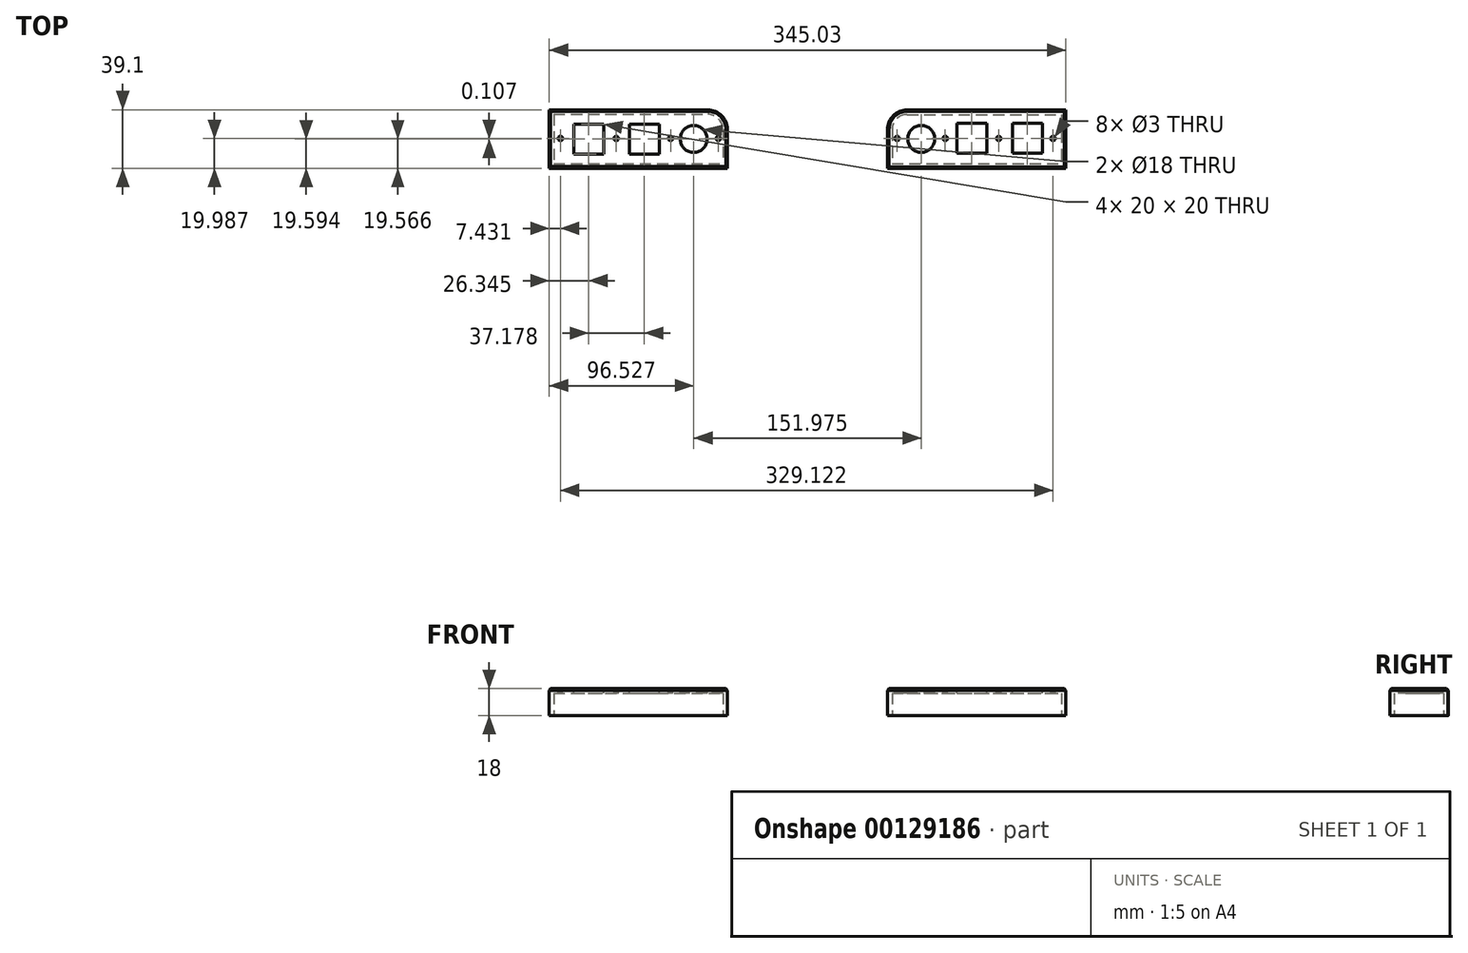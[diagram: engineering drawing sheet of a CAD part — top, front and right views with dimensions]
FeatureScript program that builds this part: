
annotation { "Feature Type Name" : "Feature", "Feature Type Description" : "" }
export const myFeature = defineFeature(function(context is Context, id is Id, definition is map)
    precondition{}
    {
        {
            var Q0;
            Q0=qCreatedBy(makeId("Top.planeOp"),FACE);
            var sketch = newSketch(context, id + "F0", { "sketchPlane" : qUnion([Q0])});
            skLineSegment(sketch, "E0.bottom", {"start": v(66.11, 78.9) * mm, "end": v(169.11, 78.9) * mm});
            skLineSegment(sketch, "E0.top", {"start": v(56.11, 45.9) * mm, "end": v(169.11, 45.9) * mm});
            skLineSegment(sketch, "E0.left", {"start": v(56.11, 68.9) * mm, "end": v(56.11, 45.9) * mm});
            skLineSegment(sketch, "E0.right", {"start": v(169.11, 78.9) * mm, "end": v(169.11, 45.9) * mm});
            skLineSegment(sketch, "E1.bottom", {"start": v(-169.92, 79) * mm, "end": v(-66.92, 79) * mm});
            skLineSegment(sketch, "E1.top", {"start": v(-169.92, 46) * mm, "end": v(-56.92, 46) * mm});
            skLineSegment(sketch, "E1.left", {"start": v(-169.92, 79) * mm, "end": v(-169.92, 46) * mm});
            skLineSegment(sketch, "E1.right", {"start": v(-56.92, 69) * mm, "end": v(-56.92, 46) * mm});
            skPoint(sketch, "E2.visualSharp", {"position": v(-56.92, 79) * mm});
            skArc(sketch, "E2.filletArc", {"start": v(-56.92, 69) * mm, "mid": v(-59.85, 76.07) * mm, "end": v(-66.92, 79) * mm});
            skPoint(sketch, "E3.visualSharp", {"position": v(56.11, 78.9) * mm});
            skArc(sketch, "E3.filletArc", {"start": v(66.11, 78.9) * mm, "mid": v(59.04, 75.97) * mm, "end": v(56.11, 68.9) * mm});
            skSolve(sketch);
        }
        {
            var Q0;
            Q0=qSketchRegion(id+"F0",true);
            extrude(context, id + "F1", {"entities" : qUnion([Q0]), "depth" : 5 * mm, "hasSecondDirection" : true, "secondDirectionOppositeDirection" : true, "secondDirectionDepth" : 10 * mm});
        }
        {
            var Q0;
            Q0=makeQuery(id+"F1.opExtrude","CAP_FACE",FACE,{"disambiguationData":[OSD([sQuery(id+"F0.wireOp",EDGE,"E0.bottom"),sQuery(id+"F0.wireOp",EDGE,"E0.top"),sQuery(id+"F0.wireOp",EDGE,"E0.left"),sQuery(id+"F0.wireOp",EDGE,"E0.right"),sQuery(id+"F0.wireOp",EDGE,"E3.filletArc")])],"isStart":true});
            var Q1;
            Q1=makeQuery(id+"F1.opExtrude","CAP_FACE",FACE,{"disambiguationData":[OSD([sQuery(id+"F0.wireOp",EDGE,"E1.bottom"),sQuery(id+"F0.wireOp",EDGE,"E1.top"),sQuery(id+"F0.wireOp",EDGE,"E1.left"),sQuery(id+"F0.wireOp",EDGE,"E1.right"),sQuery(id+"F0.wireOp",EDGE,"E2.filletArc")])],"isStart":true});
            shell(context, id + "F2", {"entities" : qUnion([Q0, Q1]), "thickness" : 3 * mm, "oppositeDirection" : true});
        }
        {
            var Q0;
            Q0=makeQuery(id+"F1.opExtrude","CAP_FACE",FACE,{"disambiguationData":[OSD([sQuery(id+"F0.wireOp",EDGE,"E0.bottom"),sQuery(id+"F0.wireOp",EDGE,"E0.top"),sQuery(id+"F0.wireOp",EDGE,"E0.left"),sQuery(id+"F0.wireOp",EDGE,"E0.right"),sQuery(id+"F0.wireOp",EDGE,"E3.filletArc")])],"isStart":false});
            cPlane(context, id + "F3", {"entities" : qUnion([Q0]), "cplaneType" : CPlaneType.OFFSET, "offset" : 25 * mm, "width" : 150 * mm, "height" : 150 * mm});
        }
        {
            var Q0;
            Q0=qCreatedBy(id+"F3.planeOp",FACE);
            var sketch = newSketch(context, id + "F4", { "sketchPlane" : qUnion([Q0])});
            skLineSegment(sketch, "E4.bottom", {"start": v(-156.58, 72.47) * mm, "end": v(-136.58, 72.47) * mm});
            skLineSegment(sketch, "E4.top", {"start": v(-156.58, 52.47) * mm, "end": v(-136.58, 52.47) * mm});
            skLineSegment(sketch, "E4.left", {"start": v(-156.58, 72.47) * mm, "end": v(-156.58, 52.47) * mm});
            skLineSegment(sketch, "E4.right", {"start": v(-136.58, 72.47) * mm, "end": v(-136.58, 52.47) * mm});
            skLineSegment(sketch, "E5.bottom", {"start": v(-119.4, 72.47) * mm, "end": v(-99.4, 72.47) * mm});
            skLineSegment(sketch, "E5.top", {"start": v(-119.4, 52.47) * mm, "end": v(-99.4, 52.47) * mm});
            skLineSegment(sketch, "E5.left", {"start": v(-119.4, 72.47) * mm, "end": v(-119.4, 52.47) * mm});
            skLineSegment(sketch, "E5.right", {"start": v(-99.4, 72.47) * mm, "end": v(-99.4, 52.47) * mm});
            skCircle(sketch, "E6", {"center": v(-76.4, 62.5) * mm, "radius": 9 * mm});
            skCircle(sketch, "E7", {"center": v(75.58, 62.6) * mm, "radius": 9 * mm});
            skLineSegment(sketch, "E8.bottom", {"start": v(99.27, 72.97) * mm, "end": v(119.27, 72.97) * mm});
            skLineSegment(sketch, "E8.top", {"start": v(99.27, 52.97) * mm, "end": v(119.27, 52.97) * mm});
            skLineSegment(sketch, "E8.left", {"start": v(99.27, 72.97) * mm, "end": v(99.27, 52.97) * mm});
            skLineSegment(sketch, "E8.right", {"start": v(119.27, 72.97) * mm, "end": v(119.27, 52.97) * mm});
            skLineSegment(sketch, "E9.bottom", {"start": v(136.45, 72.97) * mm, "end": v(156.45, 72.97) * mm});
            skLineSegment(sketch, "E9.top", {"start": v(136.45, 52.97) * mm, "end": v(156.45, 52.97) * mm});
            skLineSegment(sketch, "E9.left", {"start": v(136.45, 72.97) * mm, "end": v(136.45, 52.97) * mm});
            skLineSegment(sketch, "E9.right", {"start": v(156.45, 72.97) * mm, "end": v(156.45, 52.97) * mm});
            skSolve(sketch);
        }
        {
            var Q0;
            Q0=qSketchRegion(id+"F4",true);
            extrude(context, id + "F5", {"entities" : qUnion([Q0]), "operationType" : NewBodyOperationType.REMOVE, "oppositeDirection" : true, "depth" : 50 * mm});
        }
        {
            var Q0;
            Q0=makeQuery(id+"F1.opExtrude","CAP_FACE",FACE,{"disambiguationData":[OSD([sQuery(id+"F0.wireOp",EDGE,"E1.bottom"),sQuery(id+"F0.wireOp",EDGE,"E1.top"),sQuery(id+"F0.wireOp",EDGE,"E1.left"),sQuery(id+"F0.wireOp",EDGE,"E1.right"),sQuery(id+"F0.wireOp",EDGE,"E2.filletArc")])],"isStart":false});
            cPlane(context, id + "F6", {"entities" : qUnion([Q0]), "cplaneType" : CPlaneType.OFFSET, "offset" : 0 * mm, "width" : 150 * mm, "height" : 150 * mm});
        }
        {
            var Q0;
            Q0=qCreatedBy(id+"F6.planeOp",FACE);
            var sketch = newSketch(context, id + "F7", { "sketchPlane" : qUnion([Q0])});
            skPoint(sketch, "E10", {"position": v(-165.49, 62.89) * mm});
            skPoint(sketch, "E11", {"position": v(-128.13, 62.89) * mm});
            skPoint(sketch, "E12", {"position": v(-91.87, 62.89) * mm});
            skPoint(sketch, "E13", {"position": v(-59.97, 62.89) * mm});
            skPoint(sketch, "E14", {"position": v(59.47, 62.89) * mm});
            skPoint(sketch, "E15", {"position": v(91.64, 62.89) * mm});
            skPoint(sketch, "E16", {"position": v(127.36, 62.89) * mm});
            skPoint(sketch, "E17", {"position": v(163.63, 62.89) * mm});
            skSolve(sketch);
        }
        {
            var Q0;
            Q0=sQuery(id+"F7.wireOp",VERTEX,"E11");
            var Q1;
            Q1=sQuery(id+"F7.wireOp",VERTEX,"E17");
            var Q2;
            Q2=sQuery(id+"F7.wireOp",VERTEX,"E16");
            var Q3;
            Q3=sQuery(id+"F7.wireOp",VERTEX,"E10");
            var Q4;
            Q4=sQuery(id+"F7.wireOp",VERTEX,"E15");
            var Q5;
            Q5=sQuery(id+"F7.wireOp",VERTEX,"E14");
            var Q6;
            Q6=sQuery(id+"F7.wireOp",VERTEX,"E12");
            var Q7;
            Q7=sQuery(id+"F7.wireOp",VERTEX,"E13");
            var Q8;
            Q8=makeQuery(id+"F1.opExtrude","SWEPT_BODY",BODY,{"disambiguationData":[OSD([sQuery(id+"F0.wireOp",EDGE,"E0.bottom"),sQuery(id+"F0.wireOp",EDGE,"E0.top"),sQuery(id+"F0.wireOp",EDGE,"E0.left"),sQuery(id+"F0.wireOp",EDGE,"E0.right"),sQuery(id+"F0.wireOp",EDGE,"E3.filletArc")])]});
            var Q9;
            Q9=makeQuery(id+"F1.opExtrude","SWEPT_BODY",BODY,{"disambiguationData":[OSD([sQuery(id+"F0.wireOp",EDGE,"E1.bottom"),sQuery(id+"F0.wireOp",EDGE,"E1.top"),sQuery(id+"F0.wireOp",EDGE,"E1.left"),sQuery(id+"F0.wireOp",EDGE,"E1.right"),sQuery(id+"F0.wireOp",EDGE,"E2.filletArc")])]});
            hole(context, id + "F8", {"style" : HoleStyle.SIMPLE, "endStyle" : HoleEndStyle.BLIND, "holeDiameter" : 3 * mm, "holeDepth" : 40 * mm, "startFromSketch" : true, "locations" : qUnion([Q0, Q1, Q2, Q3, Q4, Q5, Q6, Q7]), "scope" : qUnion([Q8, Q9])});
        }
        {
            var Q0;
            Q0=makeQuery(id+"F1.opExtrude","CAP_EDGE",EDGE,{"disambiguationData":[OSD([sQuery(id+"F0.wireOp",EDGE,"E1.top")])],"isStart":false});
            var Q1;
            Q1=makeQuery(id+"F1.opExtrude","CAP_EDGE",EDGE,{"disambiguationData":[OSD([sQuery(id+"F0.wireOp",EDGE,"E1.left")])],"isStart":false});
            var Q2;
            Q2=makeQuery(id+"F1.opExtrude","CAP_EDGE",EDGE,{"disambiguationData":[OSD([sQuery(id+"F0.wireOp",EDGE,"E1.bottom")])],"isStart":false});
            var Q3;
            Q3=makeQuery(id+"F1.opExtrude","CAP_EDGE",EDGE,{"disambiguationData":[OSD([sQuery(id+"F0.wireOp",EDGE,"E0.left")])],"isStart":false});
            var Q4;
            Q4=makeQuery(id+"F1.opExtrude","CAP_EDGE",EDGE,{"disambiguationData":[OSD([sQuery(id+"F0.wireOp",EDGE,"E0.top")])],"isStart":false});
            var Q5;
            Q5=makeQuery(id+"F1.opExtrude","CAP_EDGE",EDGE,{"disambiguationData":[OSD([sQuery(id+"F0.wireOp",EDGE,"E0.right")])],"isStart":false});
            chamfer(context, id + "F9", {"entities" : qUnion([Q0, Q1, Q2, Q3, Q4, Q5]), "width" : 1 * mm, "tangentPropagation" : true});
        }
    });
